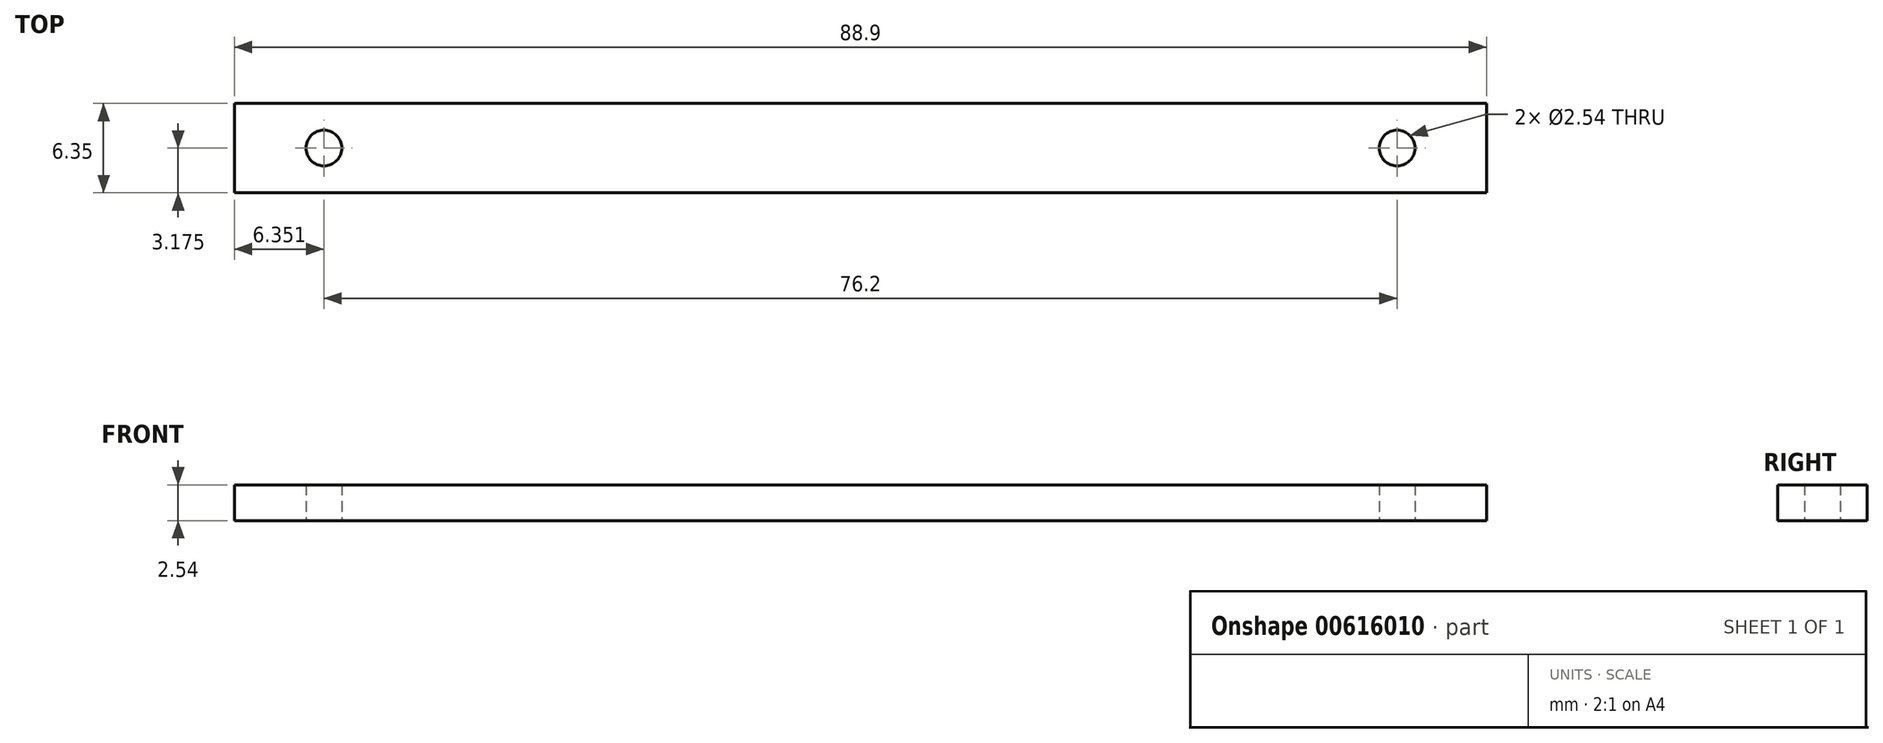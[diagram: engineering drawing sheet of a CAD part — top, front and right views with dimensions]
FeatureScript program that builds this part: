
annotation { "Feature Type Name" : "Feature", "Feature Type Description" : "" }
export const myFeature = defineFeature(function(context is Context, id is Id, definition is map)
    precondition{}
    {
        {
            var Q0;
            Q0=qCreatedBy(makeId("Top.planeOp"),FACE);
            var sketch = newSketch(context, id + "F0", { "sketchPlane" : qUnion([Q0])});
            skLineSegment(sketch, "E0.bottom", {"start": v(-28.29, -7.3) * mm, "end": v(60.61, -7.3) * mm});
            skLineSegment(sketch, "E0.top", {"start": v(-28.29, -13.64) * mm, "end": v(60.61, -13.64) * mm});
            skLineSegment(sketch, "E0.left", {"start": v(-28.29, -7.3) * mm, "end": v(-28.29, -13.64) * mm});
            skLineSegment(sketch, "E0.right", {"start": v(60.61, -7.3) * mm, "end": v(60.61, -13.64) * mm});
            skCircle(sketch, "E1", {"center": v(-21.94, -10.47) * mm, "radius": 1.27 * mm});
            skCircle(sketch, "E2", {"center": v(54.26, -10.47) * mm, "radius": 1.27 * mm});
            skSolve(sketch);
        }
        {
            var Q0;
            Q0 = qSketchRegion(id + "F0", true);
            extrude(context, id + "F1", {"entities" : qUnion([Q0]), "depth" : 2.54 * mm, "offsetDistance" : 25.4 * mm});
        }
    });
